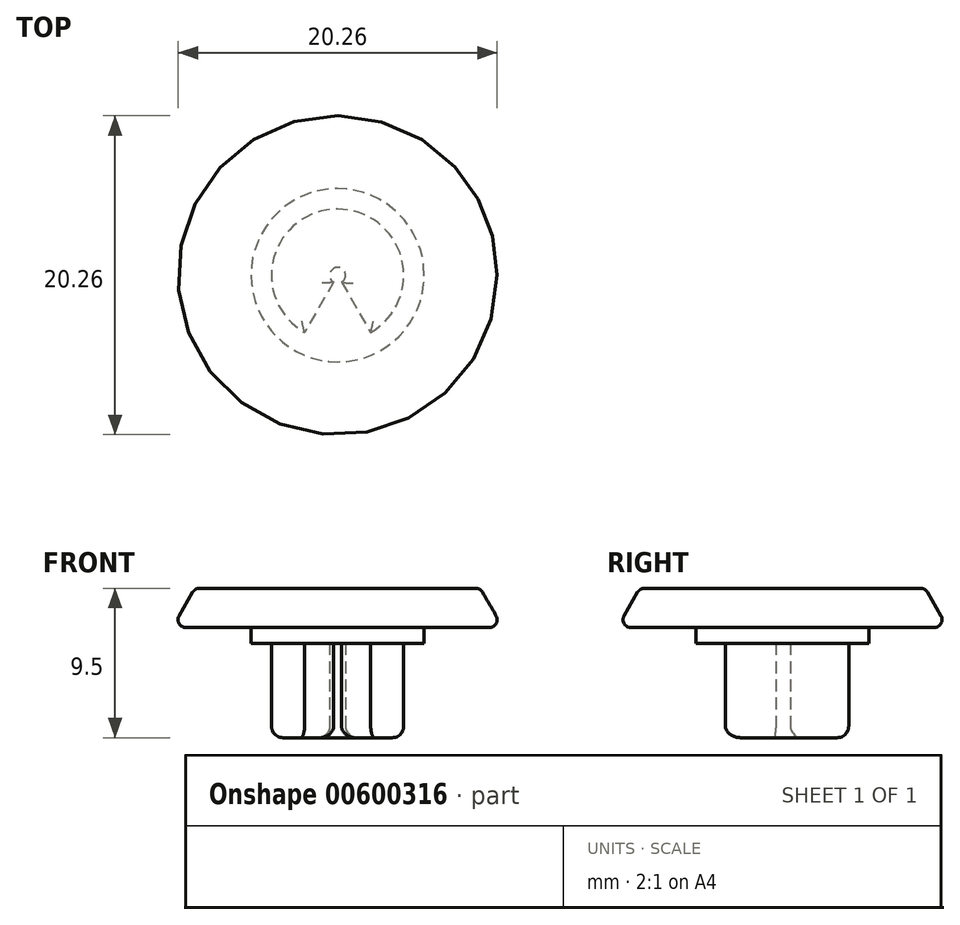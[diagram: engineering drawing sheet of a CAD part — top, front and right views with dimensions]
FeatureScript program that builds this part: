
annotation { "Feature Type Name" : "Feature", "Feature Type Description" : "" }
export const myFeature = defineFeature(function(context is Context, id is Id, definition is map)
    precondition{}
    {
        {
            var Q0;
            Q0=qCreatedBy(makeId("Front.planeOp"),FACE);
            var sketch = newSketch(context, id + "F0", { "sketchPlane" : qUnion([Q0])});
            skLineSegment(sketch, "E0", {"start": v(5.5, 6) * mm, "end": v(5.5, 7) * mm});
            skLineSegment(sketch, "E1", {"start": v(5.5, 7) * mm, "end": v(10.5, 7) * mm});
            skLineSegment(sketch, "E2", {"start": v(0, 9.5) * mm, "end": v(0, 0) * mm});
            skLineSegment(sketch, "E3", {"start": v(5.5, 6) * mm, "end": v(4.2, 6) * mm});
            skLineSegment(sketch, "E4", {"start": v(4.2, 6) * mm, "end": v(4.2, 0) * mm});
            skLineSegment(sketch, "E5", {"start": v(4.2, 0) * mm, "end": v(0, 0) * mm});
            skPoint(sketch, "E6.orphan", {"position": v(0, 0) * mm});
            skLineSegment(sketch, "E7", {"start": v(10.5, 7) * mm, "end": v(9.06, 9.5) * mm});
            skLineSegment(sketch, "E8", {"start": v(9.06, 9.5) * mm, "end": v(0, 9.5) * mm});
            skSolve(sketch);
        }
        {
            var Q0;
            Q0=qSketchRegion(id+"F0",true);
            var Q1;
            Q1=sQuery(id+"F0.wireOp",EDGE,"E2");
            revolve(context, id + "F1", {"entities" : qUnion([Q0]), "axis" : qUnion([Q1]), "revolveType" : RevolveType.FULL});
        }
        {
            var Q0;
            Q0=makeQuery(id+"F1.opRevolve","SWEPT_FACE",FACE,{"disambiguationData":[OSD([sQuery(id+"F0.wireOp",EDGE,"E5")])]});
            var sketch = newSketch(context, id + "F2", { "sketchPlane" : qUnion([Q0])});
            skArc(sketch, "E9", {"start": v(-0.25, 0.43) * mm, "mid": v(0, -0.5) * mm, "end": v(0.25, 0.43) * mm});
            skArc(sketch, "E10.0", {"start": v(2.1, 3.64) * mm, "mid": v(0, 4.2) * mm, "end": v(-2.1, 3.64) * mm});
            skLineSegment(sketch, "E11", {"start": v(-2.1, 3.64) * mm, "end": v(-0.25, 0.43) * mm});
            skLineSegment(sketch, "E12", {"start": v(2.1, 3.64) * mm, "end": v(0.25, 0.43) * mm});
            skSolve(sketch);
        }
        {
            var Q0;
            Q0=qSketchRegion(id+"F2",true);
            var Q1;
            Q1=makeQuery(id+"F1.opRevolve","SWEPT_FACE",FACE,{"disambiguationData":[OSD([sQuery(id+"F0.wireOp",EDGE,"E3")])]});
            extrude(context, id + "F3", {"entities" : qUnion([Q0]), "operationType" : NewBodyOperationType.REMOVE, "endBound" : BoundingType.UP_TO_SURFACE, "oppositeDirection" : true, "depth" : 25 * mm, "endBoundEntityFace" : qUnion([Q1]), "offsetDistance" : 25 * mm});
        }
        {
            var Q0;
            {var subQ2=makeQuery(id+"F3.boolean.opBoolean","COPY",FACE,{"derivedFrom":makeQuery(id+"F3.opExtrude","SWEPT_FACE",FACE,{"disambiguationData":[OSD([sQuery(id+"F2.wireOp",EDGE,"E11")])]})});Q0=makeQuery(id+"Fmqv6moUgZnORJw_2.2.F3.boolean.opBoolean","SPLIT",FACE,{"disambiguationData":[TD([subQ2])],"derivedFrom":makeQuery(id+"Fmqv6moUgZnORJw_2.1.F3.boolean.opBoolean","SPLIT",FACE,{"disambiguationData":[TD([subQ2])],"derivedFrom":makeQuery(id+"F1.opRevolve","SWEPT_FACE",FACE,{"disambiguationData":[OSD([sQuery(id+"F0.wireOp",EDGE,"E5")])]})})});}
            var Q1;
            {var subQ1=makeQuery(id+"Fmqv6moUgZnORJw_2.1.F3.opExtrude","SWEPT_FACE",FACE,{"disambiguationData":[OSD([sQuery(id+"F2.wireOp",EDGE,"E12")])]});var subQ3=sQuery(id+"F2.wireOp",EDGE,"E11");Q1=makeQuery(id+"Fmqv6moUgZnORJw_2.2.F3.boolean.opBoolean","SPLIT",FACE,{"disambiguationData":[TD([makeQuery(id+"Fmqv6moUgZnORJw_2.1.F3.boolean.opBoolean","COPY",FACE,{"derivedFrom":subQ1})])],"derivedFrom":makeQuery(id+"Fmqv6moUgZnORJw_2.1.F3.boolean.opBoolean","SPLIT",FACE,{"disambiguationData":[TD([makeQuery(id+"F3.boolean.opBoolean","COPY",FACE,{"derivedFrom":makeQuery(id+"F3.opExtrude","SWEPT_FACE",FACE,{"disambiguationData":[OSD([subQ3])]})})])],"derivedFrom":makeQuery(id+"F1.opRevolve","SWEPT_FACE",FACE,{"disambiguationData":[OSD([sQuery(id+"F0.wireOp",EDGE,"E5")])]})})});}
            var Q2;
            Q2=makeQuery(id+"Fmqv6moUgZnORJw_2.1.F3.boolean.opBoolean","SPLIT",FACE,{"disambiguationData":[TD([makeQuery(id+"F3.boolean.opBoolean","COPY",FACE,{"derivedFrom":makeQuery(id+"F3.opExtrude","SWEPT_FACE",FACE,{"disambiguationData":[OSD([sQuery(id+"F2.wireOp",EDGE,"E12")])]})})])],"derivedFrom":makeQuery(id+"F1.opRevolve","SWEPT_FACE",FACE,{"disambiguationData":[OSD([sQuery(id+"F0.wireOp",EDGE,"E5")])]})});
            fillet(context, id + "F4", {"entities" : qUnion([Q0, Q1, Q2]), "radius" : .75 * mm, "tangentPropagation" : true, "allowEdgeOverflow" : false});
        }
        {
            var Q0;
            Q0=makeQuery(id+"F1.opRevolve","SWEPT_EDGE",EDGE,{"disambiguationData":[OSD([sQuery(id+"F0.wireOp",EDGE,"E7"),sQuery(id+"F0.wireOp",EDGE,"E8")])]});
            var Q1;
            Q1=makeQuery(id+"F1.opRevolve","SWEPT_EDGE",EDGE,{"disambiguationData":[OSD([sQuery(id+"F0.wireOp",EDGE,"E1"),sQuery(id+"F0.wireOp",EDGE,"E7")])]});
            fillet(context, id + "F5", {"entities" : qUnion([Q0, Q1]), "radius" : .5 * mm, "tangentPropagation" : true, "allowEdgeOverflow" : false});
        }
    });
